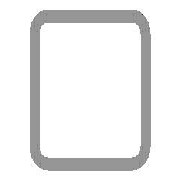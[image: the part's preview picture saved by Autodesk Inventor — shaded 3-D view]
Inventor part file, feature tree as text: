
AUTODESK INVENTOR PART (.ipt)
format: ipt  version: 2025 (Build 290162010, 162A)  size: 134,656 bytes
history: native  units: mm (DEFAULTED — no unit token found)
features: other x4, sketch x1, plane x1
ambient origin geometry x8: Origin, YZ Plane, XZ Plane, XY Plane, X Axis, Y Axis, Z Axis, Center Point
bodies: Solid1 (feature_tree), Body (feature_tree)
feature tree (6):
  parser-record x1  (decoder bookkeeping rows leaked as tree rows — omitted from the tree; the rows remain in map.json)
  other  "Driven Length"
  other  "Start Plane"
  other  "End Plane"
  sketch  "Sketch3"  dims[d3=758.0mm d4=0.0mm d7=6.0mm d9=80.0mm d11=80.0mm d12=3.0mm d13=-0.0mm d14=758.0mm d15=40.0mm d16=40.0mm d17=90.0deg d18=758.0mm]
  plane  "Work Plane3"
